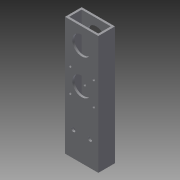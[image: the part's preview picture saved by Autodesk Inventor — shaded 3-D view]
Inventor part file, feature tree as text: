
AUTODESK INVENTOR PART (.ipt)
format: ipt  version: 2013 (Build 170138000, 138)  size: 140,288 bytes
history: native  units: in
note: dims shown in document units (in); Inventor stores cm internally (conversion verified against a paired STEP export)
features: extrude x3, sketch x3
ambient origin geometry x8: Origin, YZ Plane, XZ Plane, XY Plane, X Axis, Y Axis, Z Axis, Center Point
bodies: Solid1 (feature_tree)
feature tree (6):
  extrude  "Extrusion1"  Depth=1.0in
  extrude  "Extrusion2"  Depth=0.75in
  extrude  "Extrusion3"  Depth=1.5in
  sketch  "Sketch1"  dims[d0=2.0in d1=1.0in]
  sketch  "Sketch2"  dims[d2=1.75in d3=0.75in]
  sketch  "Sketch3"  dims[d4=7.125in d5=0.0in d6=1.5in d8=0.5in d9=0.0in d10=1.0in d11=180.0deg d12=0.25in d13=0.25in d14=1.0in d15=90.0deg d16=1.125in d17=7.125in d18=0.0in d19=4.0in d20=90.0deg d21=1.125in d22=1.0in d23=45.0deg d24=2.0in d25=0.0in d26=0.16in d27=0.16in d28=0.16in d29=0.16in d30=7.125in d31=0.0in]
